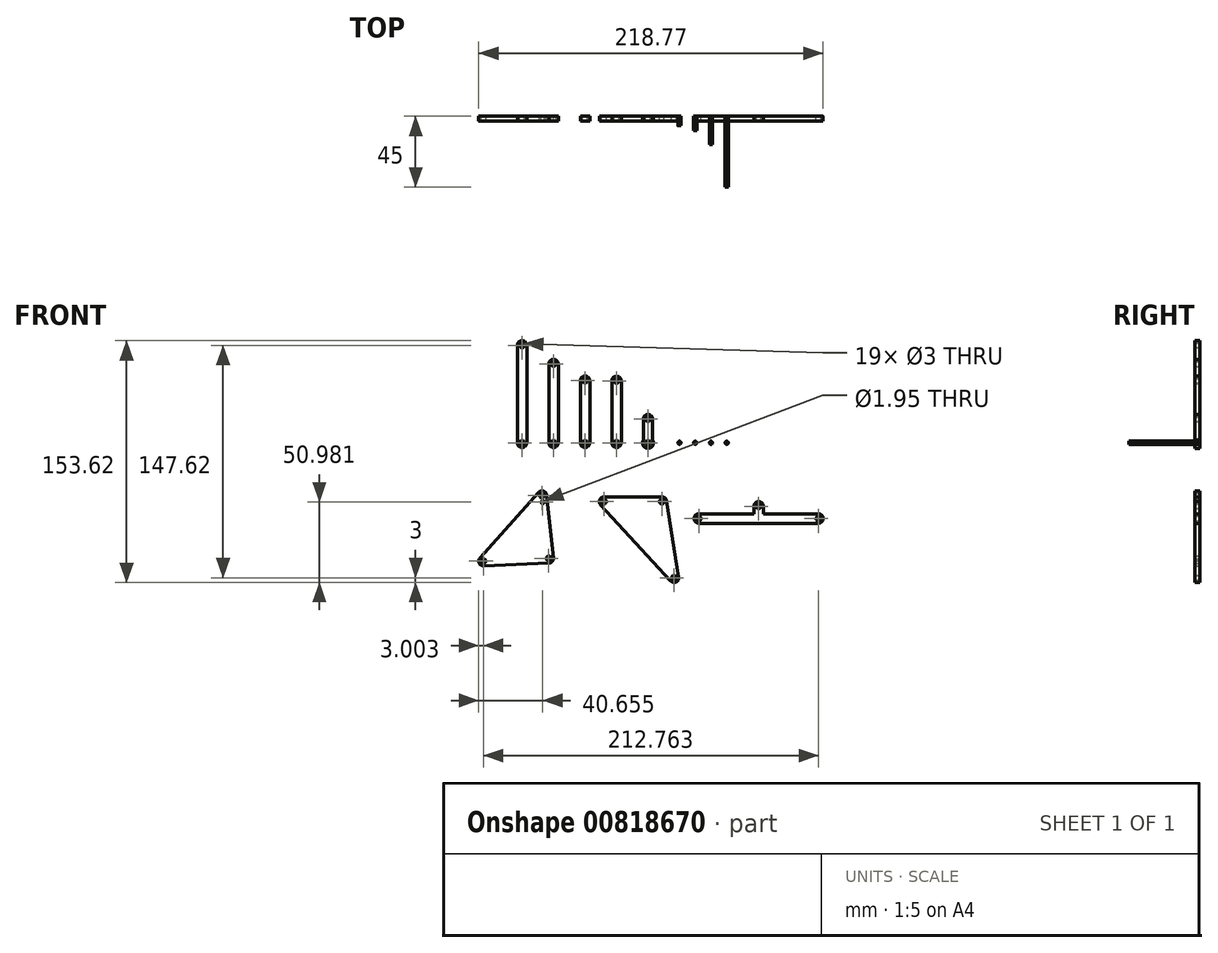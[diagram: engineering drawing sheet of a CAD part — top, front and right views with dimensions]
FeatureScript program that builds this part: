
annotation { "Feature Type Name" : "Feature", "Feature Type Description" : "" }
export const myFeature = defineFeature(function(context is Context, id is Id, definition is map)
    precondition{}
    {
        {
            var Q0;
            Q0=qCreatedBy(makeId("Front.planeOp"),FACE);
            var sketch = newSketch(context, id + "F0", { "sketchPlane" : qUnion([Q0])});
            skArc(sketch, "E0", {"start": v(-7, 15) * mm, "mid": v(-10, 18) * mm, "end": v(-13, 15) * mm});
            skLineSegment(sketch, "E1", {"start": v(-7, 15) * mm, "end": v(-7, 1.8) * mm});
            skCircle(sketch, "E2", {"center": v(-10, 15) * mm, "radius": 1.5 * mm});
            skCircle(sketch, "E3", {"center": v(-10, 0) * mm, "radius": 1.5 * mm});
            skArc(sketch, "E4", {"start": v(-33, 0) * mm, "mid": v(-30, -3) * mm, "end": v(-27, 0) * mm});
            skArc(sketch, "E5", {"start": v(-27, 39.3) * mm, "mid": v(-30, 42.3) * mm, "end": v(-33, 39.3) * mm});
            skLineSegment(sketch, "E6", {"start": v(-33, 39.3) * mm, "end": v(-33, 0) * mm});
            skLineSegment(sketch, "E7", {"start": v(-27, 39.3) * mm, "end": v(-27, 0) * mm});
            skCircle(sketch, "E8", {"center": v(-30, 39.3) * mm, "radius": 1.5 * mm});
            skCircle(sketch, "E9", {"center": v(-30, 0) * mm, "radius": 1.5 * mm});
            skArc(sketch, "E10", {"start": v(-53, 0) * mm, "mid": v(-50, -3) * mm, "end": v(-47, 0) * mm});
            skArc(sketch, "E11", {"start": v(-47, 39.4) * mm, "mid": v(-50, 42.4) * mm, "end": v(-53, 39.4) * mm});
            skLineSegment(sketch, "E12", {"start": v(-53, 39.4) * mm, "end": v(-53, 0) * mm});
            skLineSegment(sketch, "E13", {"start": v(-47, 39.4) * mm, "end": v(-47, 0) * mm});
            skCircle(sketch, "E14", {"center": v(-50, 39.4) * mm, "radius": 1.5 * mm});
            skCircle(sketch, "E15", {"center": v(-50, 0) * mm, "radius": 1.5 * mm});
            skArc(sketch, "E16", {"start": v(-73, 0) * mm, "mid": v(-70, -3) * mm, "end": v(-67, 0) * mm});
            skArc(sketch, "E17", {"start": v(-67, 50) * mm, "mid": v(-70, 53) * mm, "end": v(-73, 50) * mm});
            skLineSegment(sketch, "E18", {"start": v(-73, 50) * mm, "end": v(-73, 0) * mm});
            skLineSegment(sketch, "E19", {"start": v(-67, 50) * mm, "end": v(-67, 0) * mm});
            skCircle(sketch, "E20", {"center": v(-70, 50) * mm, "radius": 1.5 * mm});
            skCircle(sketch, "E21", {"center": v(-70, 0) * mm, "radius": 1.5 * mm});
            skArc(sketch, "E22", {"start": v(-93, 0) * mm, "mid": v(-90, -3) * mm, "end": v(-87, 0) * mm});
            skArc(sketch, "E23", {"start": v(-87, 61.9) * mm, "mid": v(-90, 64.9) * mm, "end": v(-93, 61.9) * mm});
            skLineSegment(sketch, "E24", {"start": v(-93, 61.9) * mm, "end": v(-93, 0) * mm});
            skLineSegment(sketch, "E25", {"start": v(-87, 61.9) * mm, "end": v(-87, 0) * mm});
            skCircle(sketch, "E26", {"center": v(-90, 61.9) * mm, "radius": 1.5 * mm});
            skCircle(sketch, "E27", {"center": v(-90, 0) * mm, "radius": 1.5 * mm});
            skLineSegment(sketch, "E28", {"start": v(-77.3, -33.58) * mm, "end": v(-114.52, -75.16) * mm, "construction": true});
            skLineSegment(sketch, "E29", {"start": v(-114.52, -75.16) * mm, "end": v(-73.05, -73.45) * mm, "construction": true});
            skLineSegment(sketch, "E30", {"start": v(-73.05, -73.45) * mm, "end": v(-77.3, -33.58) * mm, "construction": true});
            skArc(sketch, "E31", {"start": v(-74.33, -33.26) * mm, "mid": v(-76.39, -30.72) * mm, "end": v(-79.55, -31.58) * mm});
            skArc(sketch, "E32", {"start": v(-72.93, -76.45) * mm, "mid": v(-70.78, -75.4) * mm, "end": v(-70.07, -73.13) * mm});
            skArc(sketch, "E33", {"start": v(-116.75, -73.16) * mm, "mid": v(-117.23, -76.44) * mm, "end": v(-114.4, -78.16) * mm});
            skLineSegment(sketch, "E34", {"start": v(-116.75, -73.16) * mm, "end": v(-79.55, -31.58) * mm});
            skLineSegment(sketch, "E35", {"start": v(-114.4, -78.16) * mm, "end": v(-72.93, -76.45) * mm});
            skLineSegment(sketch, "E36", {"start": v(-74.33, -33.26) * mm, "end": v(-70.07, -73.13) * mm});
            skCircle(sketch, "E37", {"center": v(-114.52, -75.16) * mm, "radius": 1.5 * mm});
            skCircle(sketch, "E38", {"center": v(-73.05, -73.45) * mm, "radius": 1.5 * mm});
            skCircle(sketch, "E39", {"center": v(-77.3, -33.58) * mm, "radius": 1.5 * mm});
            skCircle(sketch, "E40", {"center": v(-76.87, -37.74) * mm, "radius": 0.98 * mm});
            skLineSegment(sketch, "E41", {"start": v(-37.9, -37.34) * mm, "end": v(-1.2, -37.34) * mm, "construction": true});
            skLineSegment(sketch, "E42", {"start": v(-1.2, -37.34) * mm, "end": v(6.54, -85.72) * mm, "construction": true});
            skLineSegment(sketch, "E43", {"start": v(6.54, -85.72) * mm, "end": v(-37.9, -37.34) * mm, "construction": true});
            skArc(sketch, "E44", {"start": v(-37.9, -34.34) * mm, "mid": v(-40.65, -36.13) * mm, "end": v(-40.11, -39.37) * mm});
            skArc(sketch, "E45", {"start": v(1.76, -36.86) * mm, "mid": v(0.74, -35.05) * mm, "end": v(-1.2, -34.34) * mm});
            skArc(sketch, "E46", {"start": v(4.33, -87.75) * mm, "mid": v(7.85, -88.42) * mm, "end": v(9.5, -85.25) * mm});
            skLineSegment(sketch, "E47", {"start": v(-40.11, -39.37) * mm, "end": v(4.33, -87.75) * mm});
            skLineSegment(sketch, "E48", {"start": v(9.5, -85.25) * mm, "end": v(1.76, -36.86) * mm});
            skLineSegment(sketch, "E49", {"start": v(-37.9, -34.34) * mm, "end": v(-1.2, -34.34) * mm});
            skCircle(sketch, "E50", {"center": v(-37.9, -37.34) * mm, "radius": 1.5 * mm});
            skCircle(sketch, "E51", {"center": v(-1.2, -37.34) * mm, "radius": 1.5 * mm});
            skCircle(sketch, "E52", {"center": v(6.54, -85.72) * mm, "radius": 1.5 * mm});
            skLineSegment(sketch, "E53", {"start": v(22.25, -48.14) * mm, "end": v(60.25, -48.14) * mm, "construction": true});
            skLineSegment(sketch, "E54", {"start": v(98.25, -48.14) * mm, "end": v(60.25, -48.14) * mm, "construction": true});
            skLineSegment(sketch, "E55", {"start": v(60.25, -48.14) * mm, "end": v(60.25, -40.34) * mm, "construction": true});
            skArc(sketch, "E56", {"start": v(22.25, -45.14) * mm, "mid": v(19.25, -48.14) * mm, "end": v(22.25, -51.14) * mm});
            skArc(sketch, "E57", {"start": v(98.25, -51.14) * mm, "mid": v(101.25, -48.14) * mm, "end": v(98.25, -45.14) * mm});
            skArc(sketch, "E58", {"start": v(63.25, -40.34) * mm, "mid": v(60.25, -37.34) * mm, "end": v(57.25, -40.34) * mm});
            skLineSegment(sketch, "E59", {"start": v(22.25, -51.14) * mm, "end": v(98.25, -51.14) * mm});
            skLineSegment(sketch, "E60", {"start": v(22.25, -45.14) * mm, "end": v(57.25, -45.14) * mm});
            skLineSegment(sketch, "E61", {"start": v(57.25, -40.34) * mm, "end": v(57.25, -45.14) * mm});
            skLineSegment(sketch, "E62.MirrorCS", {"start": v(63.25, -40.34) * mm, "end": v(63.25, -45.14) * mm});
            skLineSegment(sketch, "E63.MirrorCS", {"start": v(98.25, -45.14) * mm, "end": v(63.25, -45.14) * mm});
            skCircle(sketch, "E64", {"center": v(60.25, -40.34) * mm, "radius": 1.5 * mm});
            skCircle(sketch, "E65", {"center": v(22.25, -48.14) * mm, "radius": 1.5 * mm});
            skCircle(sketch, "E66", {"center": v(98.25, -48.14) * mm, "radius": 1.5 * mm});
            skLineSegment(sketch, "E67", {"start": v(-13, 15) * mm, "end": v(-13, 1.8) * mm});
            skArc(sketch, "E68", {"start": v(-13, 1.8) * mm, "mid": v(-10, -3.5) * mm, "end": v(-7, 1.8) * mm});
            skSolve(sketch);
        }
        {
            assignVariable(context, id + "F1", {"name" : "thinkress", "anyValue" : 3});
        }
        {
            var Q0;
            Q0=makeQuery(id+"F0.imprint","IMPRINT",FACE,{"disambiguationData":[TD([[makeQuery(id+"F0.imprint","IMPRINT",EDGE,{"derivedFrom":sQuery(id+"F0.wireOp",EDGE,"E22")}),1.0]])]});
            var Q1;
            Q1=makeQuery(id+"F0.imprint","IMPRINT",FACE,{"disambiguationData":[TD([[makeQuery(id+"F0.imprint","IMPRINT",EDGE,{"derivedFrom":sQuery(id+"F0.wireOp",EDGE,"E16")}),1.0]])]});
            var Q2;
            Q2=makeQuery(id+"F0.imprint","IMPRINT",FACE,{"disambiguationData":[TD([[makeQuery(id+"F0.imprint","IMPRINT",EDGE,{"derivedFrom":sQuery(id+"F0.wireOp",EDGE,"E10")}),1.0]])]});
            var Q3;
            Q3=makeQuery(id+"F0.imprint","IMPRINT",FACE,{"disambiguationData":[TD([[makeQuery(id+"F0.imprint","IMPRINT",EDGE,{"derivedFrom":sQuery(id+"F0.wireOp",EDGE,"E4")}),1.0]])]});
            var Q4;
            Q4=makeQuery(id+"F0.imprint","IMPRINT",FACE,{"disambiguationData":[TD([[makeQuery(id+"F0.imprint","IMPRINT",EDGE,{"derivedFrom":sQuery(id+"F0.wireOp",EDGE,"pFGHl5MR-W3qR-0Xu0-SkIq-0BzEdmV8e8ho")}),1.0]])]});
            var Q5;
            Q5=makeQuery(id+"F0.imprint","IMPRINT",FACE,{"disambiguationData":[TD([[makeQuery(id+"F0.imprint","IMPRINT",EDGE,{"derivedFrom":sQuery(id+"F0.wireOp",EDGE,"E31")}),1.0]])]});
            var Q6;
            Q6=makeQuery(id+"F0.imprint","IMPRINT",FACE,{"disambiguationData":[TD([[makeQuery(id+"F0.imprint","IMPRINT",EDGE,{"derivedFrom":sQuery(id+"F0.wireOp",EDGE,"E44")}),1.0]])]});
            var Q7;
            Q7=makeQuery(id+"F0.imprint","IMPRINT",FACE,{"disambiguationData":[TD([[makeQuery(id+"F0.imprint","IMPRINT",EDGE,{"derivedFrom":sQuery(id+"F0.wireOp",EDGE,"E56")}),1.0]])]});
            var Q8;
            Q8=makeQuery(id+"F0.imprint","IMPRINT",FACE,{"disambiguationData":[TD([[makeQuery(id+"F0.imprint","IMPRINT",EDGE,{"derivedFrom":sQuery(id+"F0.wireOp",EDGE,"E0")}),1.0]])]});
            extrude(context, id + "F2", {"entities" : qUnion([Q0, Q1, Q2, Q3, Q4, Q5, Q6, Q7, Q8]), "depth" : (getVariable(context, 'thinkress')) * mm, "offsetDistance" : 25 * mm});
        }
        {
            var Q0;
            Q0=qCreatedBy(makeId("Front.planeOp"),FACE);
            var sketch = newSketch(context, id + "F3", { "sketchPlane" : qUnion([Q0])});
            skCircle(sketch, "E69", {"center": v(10, 0) * mm, "radius": 1 * mm});
            skCircle(sketch, "E70", {"center": v(20, 0) * mm, "radius": 1 * mm});
            skCircle(sketch, "E71", {"center": v(30, 0) * mm, "radius": 1 * mm});
            skCircle(sketch, "E72", {"center": v(40, 0) * mm, "radius": 1 * mm});
            skSolve(sketch);
        }
        {
            var Q0;
            Q0=makeQuery(id+"F3.imprint","IMPRINT",FACE,{"disambiguationData":[TD([[makeQuery(id+"F3.imprint","IMPRINT",EDGE,{"derivedFrom":sQuery(id+"F3.wireOp",EDGE,"E69")}),1.0]])]});
            extrude(context, id + "F4", {"entities" : qUnion([Q0]), "depth" : (getVariable(context, 'thinkress') * 2) * mm, "offsetDistance" : 25 * mm});
        }
        {
            var Q0;
            Q0=makeQuery(id+"F3.imprint","IMPRINT",FACE,{"disambiguationData":[TD([[makeQuery(id+"F3.imprint","IMPRINT",EDGE,{"derivedFrom":sQuery(id+"F3.wireOp",EDGE,"E70")}),1.0]])]});
            extrude(context, id + "F5", {"entities" : qUnion([Q0]), "depth" : (getVariable(context, 'thinkress') * 3) * mm, "offsetDistance" : 25 * mm});
        }
        {
            var Q0;
            Q0=makeQuery(id+"F3.imprint","IMPRINT",FACE,{"disambiguationData":[TD([[makeQuery(id+"F3.imprint","IMPRINT",EDGE,{"derivedFrom":sQuery(id+"F3.wireOp",EDGE,"E71")}),1.0]])]});
            extrude(context, id + "F6", {"entities" : qUnion([Q0]), "depth" : (getVariable(context, 'thinkress') * 6) * mm, "offsetDistance" : 25 * mm});
        }
        {
            var Q0;
            Q0=makeQuery(id+"F3.imprint","IMPRINT",FACE,{"disambiguationData":[TD([[makeQuery(id+"F3.imprint","IMPRINT",EDGE,{"derivedFrom":sQuery(id+"F3.wireOp",EDGE,"E72")}),1.0]])]});
            extrude(context, id + "F7", {"entities" : qUnion([Q0]), "depth" : (getVariable(context, 'thinkress') * 15) * mm, "offsetDistance" : 25 * mm});
        }
    });
